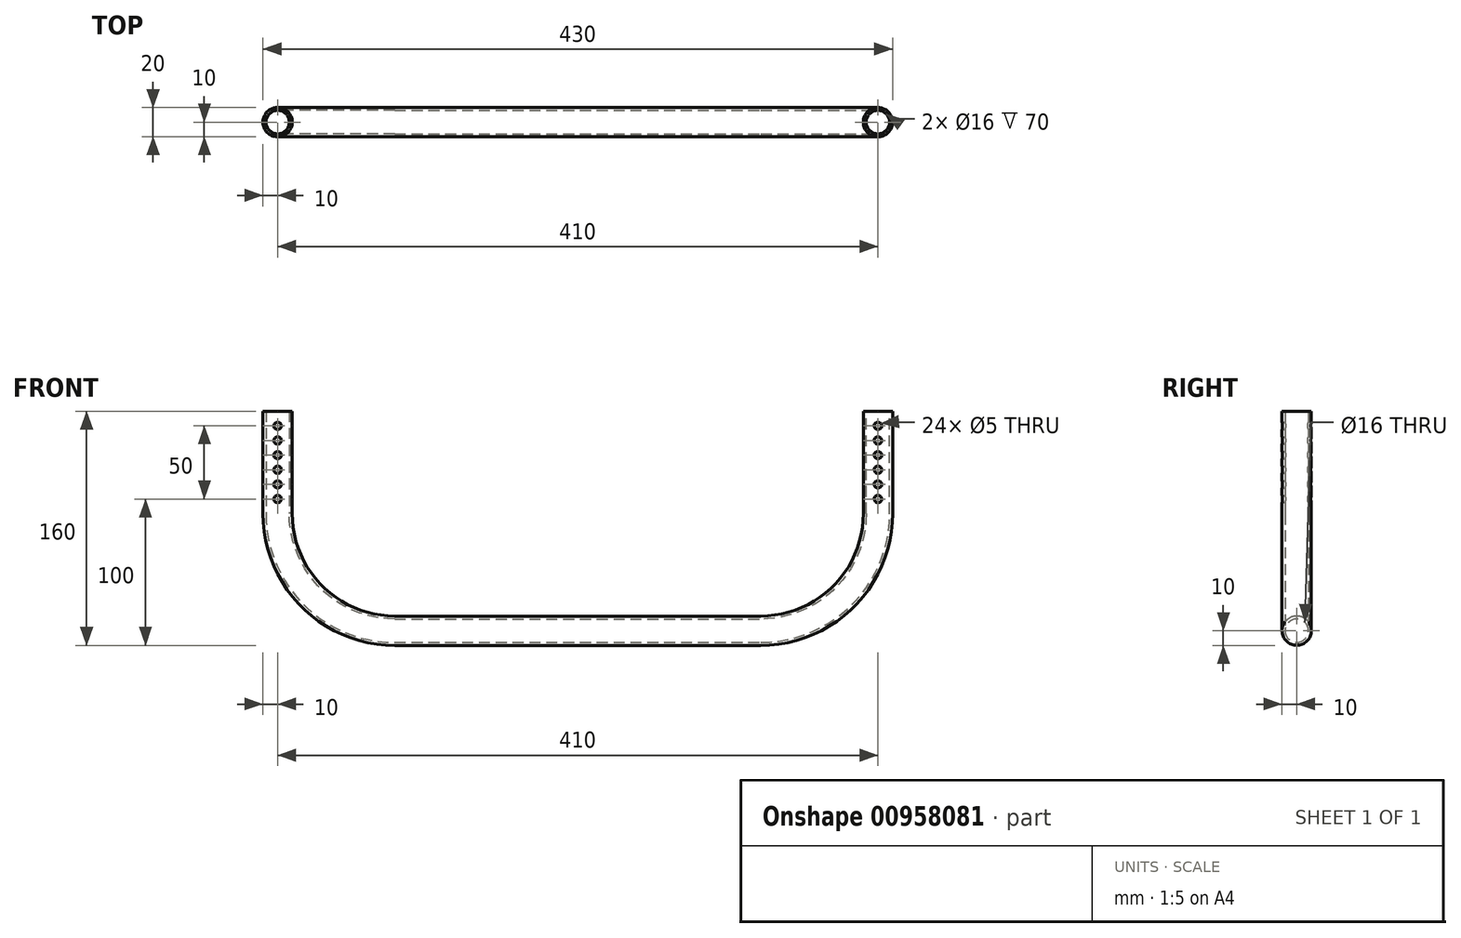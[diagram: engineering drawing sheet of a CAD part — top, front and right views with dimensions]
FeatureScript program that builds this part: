
annotation { "Feature Type Name" : "Feature", "Feature Type Description" : "" }
export const myFeature = defineFeature(function(context is Context, id is Id, definition is map)
    precondition{}
    {
        {
            var Q0;
            Q0=qCreatedBy(makeId("Front.planeOp"),FACE);
            var sketch = newSketch(context, id + "F0", { "sketchPlane" : qUnion([Q0])});
            skLineSegment(sketch, "E0", {"start": v(-205, 150) * mm, "end": v(-205, 80) * mm});
            skLineSegment(sketch, "E1", {"start": v(-125, 0) * mm, "end": v(0, 0) * mm});
            skLineSegment(sketch, "E2", {"start": v(0, 73.51) * mm, "end": v(0, -73.1) * mm, "construction": true});
            skPoint(sketch, "E3.visualSharp", {"position": v(-205, 0) * mm});
            skArc(sketch, "E3.filletArc", {"start": v(-205, 80) * mm, "mid": v(-181.57, 23.43) * mm, "end": v(-125, 0) * mm});
            skLineSegment(sketch, "E4.MirrorCS", {"start": v(205, 150) * mm, "end": v(205, 80) * mm});
            skLineSegment(sketch, "E5.MirrorCS", {"start": v(125, 0) * mm, "end": v(0, 0) * mm});
            skPoint(sketch, "E6.MirrorP", {"position": v(205, 0) * mm});
            skArc(sketch, "E7.MirrorCS", {"start": v(205, 80) * mm, "mid": v(181.57, 23.43) * mm, "end": v(125, 0) * mm});
            skPoint(sketch, "E8", {"position": v(-205, 90) * mm});
            skPoint(sketch, "E9", {"position": v(-205, 100) * mm});
            skPoint(sketch, "E10", {"position": v(-205, 110) * mm});
            skPoint(sketch, "E11", {"position": v(-205, 120) * mm});
            skPoint(sketch, "E12", {"position": v(-205, 130) * mm});
            skPoint(sketch, "E13.MirrorP", {"position": v(205, 90) * mm});
            skPoint(sketch, "E14.MirrorP", {"position": v(205, 100) * mm});
            skPoint(sketch, "E15.MirrorP", {"position": v(205, 110) * mm});
            skPoint(sketch, "E16.MirrorP", {"position": v(205, 120) * mm});
            skPoint(sketch, "E17.MirrorP", {"position": v(205, 130) * mm});
            skPoint(sketch, "E18", {"position": v(-205, 140) * mm});
            skPoint(sketch, "E19.MirrorP", {"position": v(205, 140) * mm});
            skSolve(sketch);
        }
        {
            var Q0;
            Q0=sQuery(id+"F0.wireOp",VERTEX,"E0.start");
            var Q1;
            Q1=sQuery(id+"F0.wireOp",EDGE,"E0");
            cPlane(context, id + "F1", {"entities" : qUnion([Q0, Q1]), "cplaneType" : CPlaneType.CURVE_POINT, "offset" : 25 * mm, "width" : 150 * mm, "height" : 150 * mm});
        }
        {
            var Q0;
            Q0=qCreatedBy(id+"F1.planeOp",FACE);
            var sketch = newSketch(context, id + "F2", { "sketchPlane" : qUnion([Q0])});
            skPoint(sketch, "E20.0", {"position": v(-205, 0) * mm});
            skLineSegment(sketch, "E20.2", {"start": v(-205, 0) * mm, "end": v(-125, 0) * mm});
            skLineSegment(sketch, "E20.3", {"start": v(-125, 0) * mm, "end": v(0, 0) * mm});
            skLineSegment(sketch, "E20.4", {"start": v(125, 0) * mm, "end": v(0, 0) * mm});
            skLineSegment(sketch, "E20.5", {"start": v(205, 0) * mm, "end": v(125, 0) * mm});
            skCircle(sketch, "E21", {"center": v(-205, 0) * mm, "radius": 10 * mm});
            skCircle(sketch, "E22", {"center": v(-205, 0) * mm, "radius": 8 * mm});
            skSolve(sketch);
        }
        {
            var Q0;
            Q0=makeQuery(id+"F2.imprint","IMPRINT",FACE,{"disambiguationData":[TD([[makeQuery(id+"F2.imprint","IMPRINT",EDGE,{"derivedFrom":sQuery(id+"F2.wireOp",EDGE,"E21")}),1.0]])]});
            var Q1;
            Q1=sQuery(id+"F0.wireOp",EDGE,"E0");
            var Q2;
            Q2=sQuery(id+"F0.wireOp",EDGE,"E3.filletArc");
            var Q3;
            Q3=sQuery(id+"F0.wireOp",EDGE,"E1");
            var Q4;
            Q4=sQuery(id+"F0.wireOp",EDGE,"E5.MirrorCS");
            var Q5;
            Q5=sQuery(id+"F0.wireOp",EDGE,"E7.MirrorCS");
            var Q6;
            Q6=sQuery(id+"F0.wireOp",EDGE,"E4.MirrorCS");
            sweep(context, id + "F3", {"profiles" : qUnion([Q0]), "path" : qUnion([Q1, Q2, Q3, Q4, Q5, Q6])});
        }
        {
            var Q0;
            Q0=sQuery(id+"F0.wireOp",VERTEX,"E19.MirrorP");
            var Q1;
            Q1=sQuery(id+"F0.wireOp",VERTEX,"E17.MirrorP");
            var Q2;
            Q2=sQuery(id+"F0.wireOp",VERTEX,"E16.MirrorP");
            var Q3;
            Q3=sQuery(id+"F0.wireOp",VERTEX,"E15.MirrorP");
            var Q4;
            Q4=sQuery(id+"F0.wireOp",VERTEX,"E14.MirrorP");
            var Q5;
            Q5=sQuery(id+"F0.wireOp",VERTEX,"E13.MirrorP");
            var Q6;
            Q6=sQuery(id+"F0.wireOp",VERTEX,"E18");
            var Q7;
            Q7=sQuery(id+"F0.wireOp",VERTEX,"E12");
            var Q8;
            Q8=sQuery(id+"F0.wireOp",VERTEX,"E11");
            var Q9;
            Q9=sQuery(id+"F0.wireOp",VERTEX,"E10");
            var Q10;
            Q10=sQuery(id+"F0.wireOp",VERTEX,"E9");
            var Q11;
            Q11=sQuery(id+"F0.wireOp",VERTEX,"E8");
            var Q12;
            Q12=makeQuery(id+"F3.opSweep","SWEPT_BODY",BODY,{"disambiguationData":[OSD([sQuery(id+"F0.wireOp",EDGE,"E4.MirrorCS"),sQuery(id+"F2.wireOp",EDGE,"E21"),sQuery(id+"F2.wireOp",EDGE,"E22")])]});
            hole(context, id + "F4", {"style" : HoleStyle.SIMPLE, "endStyle" : HoleEndStyle.THROUGH, "holeDiameter" : 5 * mm, "majorDiameter" : 5 * mm, "isTappedThrough" : true, "tappedDepth" : 12 * mm, "tapClearance" : 3, "locations" : qUnion([Q0, Q1, Q2, Q3, Q4, Q5, Q6, Q7, Q8, Q9, Q10, Q11]), "scope" : qUnion([Q12])});
        }
        {
            var Q0;
            Q0=sQuery(id+"F0.wireOp",VERTEX,"E18");
            var Q1;
            Q1=sQuery(id+"F0.wireOp",VERTEX,"E12");
            var Q2;
            Q2=sQuery(id+"F0.wireOp",VERTEX,"E11");
            var Q3;
            Q3=sQuery(id+"F0.wireOp",VERTEX,"E10");
            var Q4;
            Q4=sQuery(id+"F0.wireOp",VERTEX,"E9");
            var Q5;
            Q5=sQuery(id+"F0.wireOp",VERTEX,"E8");
            var Q6;
            Q6=sQuery(id+"F0.wireOp",VERTEX,"E13.MirrorP");
            var Q7;
            Q7=sQuery(id+"F0.wireOp",VERTEX,"E14.MirrorP");
            var Q8;
            Q8=sQuery(id+"F0.wireOp",VERTEX,"E15.MirrorP");
            var Q9;
            Q9=sQuery(id+"F0.wireOp",VERTEX,"E16.MirrorP");
            var Q10;
            Q10=sQuery(id+"F0.wireOp",VERTEX,"E17.MirrorP");
            var Q11;
            Q11=sQuery(id+"F0.wireOp",VERTEX,"E19.MirrorP");
            var Q12;
            Q12=makeQuery(id+"F3.opSweep","SWEPT_BODY",BODY,{"disambiguationData":[OSD([sQuery(id+"F0.wireOp",EDGE,"E4.MirrorCS"),sQuery(id+"F2.wireOp",EDGE,"E21"),sQuery(id+"F2.wireOp",EDGE,"E22")])]});
            hole(context, id + "F5", {"style" : HoleStyle.SIMPLE, "endStyle" : HoleEndStyle.THROUGH, "oppositeDirection" : true, "holeDiameter" : 5 * mm, "majorDiameter" : 5 * mm, "isTappedThrough" : true, "tappedDepth" : 12 * mm, "tapClearance" : 3, "locations" : qUnion([Q0, Q1, Q2, Q3, Q4, Q5, Q6, Q7, Q8, Q9, Q10, Q11]), "scope" : qUnion([Q12])});
        }
    });
